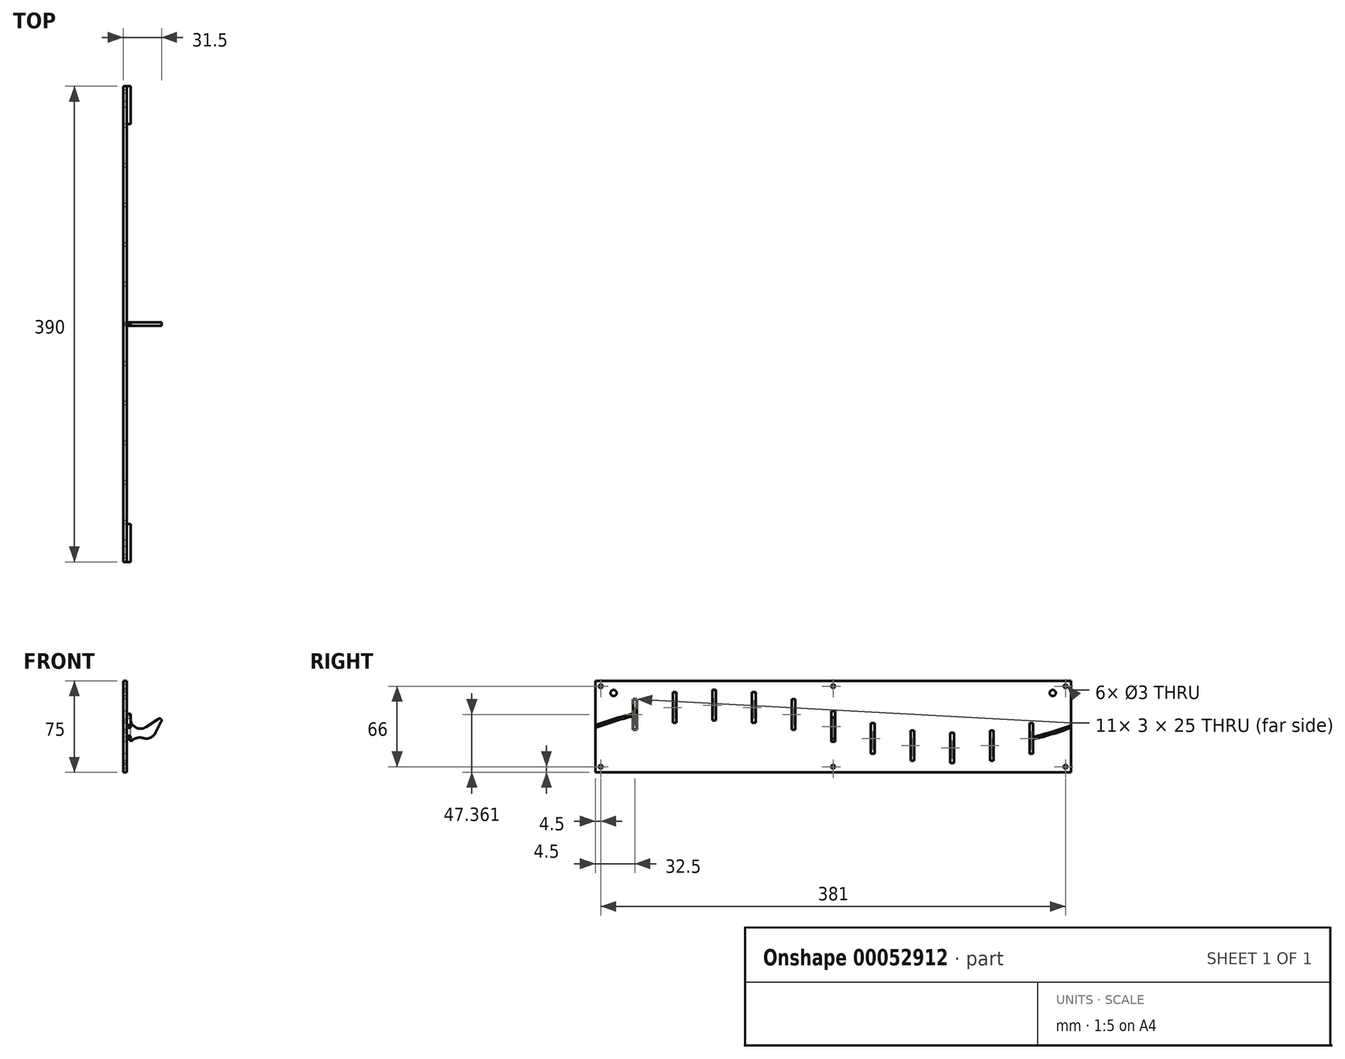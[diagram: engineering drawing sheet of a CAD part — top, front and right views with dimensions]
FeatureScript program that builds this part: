
annotation { "Feature Type Name" : "Feature", "Feature Type Description" : "" }
export const myFeature = defineFeature(function(context is Context, id is Id, definition is map)
    precondition{}
    {
        {
            assignVariable(context, id + "F0", {"name" : "Thickness", "anyValue" : 3});
        }
        {
            var Q0;
            Q0=qCreatedBy(makeId("Front.planeOp"),FACE);
            var sketch = newSketch(context, id + "F1", { "sketchPlane" : qUnion([Q0])});
            skLineSegment(sketch, "E0.top", {"start": v(0, 19) * mm, "end": v(-2, 19) * mm});
            skLineSegment(sketch, "E0.left", {"start": v(0, 0) * mm, "end": v(0, 4) * mm});
            skLineSegment(sketch, "E0.right", {"start": v(-3, 0) * mm, "end": v(-3, 3) * mm});
            skLineSegment(sketch, "E1.bottom", {"start": v(-6, 25) * mm, "end": v(-3, 25) * mm});
            skLineSegment(sketch, "E1.top", {"start": v(-6, 0) * mm, "end": v(-3, 0) * mm});
            skLineSegment(sketch, "E1.left", {"start": v(-6, 25) * mm, "end": v(-6, 0) * mm});
            skLineSegment(sketch, "E1.right", {"start": v(-3, 25) * mm, "end": v(-3, 20) * mm});
            skArc(sketch, "E2", {"start": v(-3, 20) * mm, "mid": v(-3.7, 18.3) * mm, "end": v(-2, 19) * mm});
            skLineSegment(sketch, "E3.top", {"start": v(-2, 4) * mm, "end": v(-2, 4) * mm});
            skArc(sketch, "E4", {"start": v(-2, 4) * mm, "mid": v(-3.7, 4.7) * mm, "end": v(-3, 3) * mm});
            skArc(sketch, "E5", {"start": v(0, 4) * mm, "mid": v(-1, 5) * mm, "end": v(-2, 4) * mm});
            skLineSegment(sketch, "E6.trimOffspring", {"start": v(-3, 3) * mm, "end": v(-3, 0) * mm});
            skLineSegment(sketch, "E7.trimOffspring", {"start": v(0, 19) * mm, "end": v(0, 19) * mm});
            skArc(sketch, "E8", {"start": v(0, 19) * mm, "mid": v(4.36, 11.72) * mm, "end": v(12.83, 12.13) * mm});
            skLineSegment(sketch, "E9", {"start": v(12.83, 12.13) * mm, "end": v(22.96, 18.87) * mm});
            skArc(sketch, "E10", {"start": v(25.33, 16.78) * mm, "mid": v(24.95, 18.74) * mm, "end": v(22.96, 18.87) * mm});
            skLineSegment(sketch, "E11", {"start": v(25.33, 16.78) * mm, "end": v(20.6, 7.34) * mm});
            skArc(sketch, "E12", {"start": v(10.55, 2.99) * mm, "mid": v(16.36, 3.34) * mm, "end": v(20.6, 7.34) * mm});
            skArc(sketch, "E13", {"start": v(10.55, 2.99) * mm, "mid": v(4.84, 3.02) * mm, "end": v(0, 0) * mm});
            skSolve(sketch);
        }
        {
            var Q0;
            Q0=makeQuery(id+"F1.imprint","IMPRINT",FACE,{"disambiguationData":[TD([[makeQuery(id+"F1.imprint","IMPRINT",EDGE,{"derivedFrom":sQuery(id+"F1.wireOp",EDGE,"E0.top")}),1.0]])]});
            extrude(context, id + "F2", {"entities" : qUnion([Q0]), "endBound" : BoundingType.SYMMETRIC, "depth" : (getVariable(context, 'Thickness')) * mm});
        }
        {
            var Q0;
            Q0=makeQuery(id+"F2.opExtrude","SWEPT_FACE",FACE,{"disambiguationData":[OSD([sQuery(id+"F1.wireOp",EDGE,"E1.left")])]});
            var sketch = newSketch(context, id + "F3", { "sketchPlane" : qUnion([Q0])});
            skLineSegment(sketch, "E14.bottom", {"start": v(-195, 50) * mm, "end": v(195, 50) * mm});
            skLineSegment(sketch, "E14.top", {"start": v(-195, -25) * mm, "end": v(195, -25) * mm});
            skLineSegment(sketch, "E14.left", {"start": v(-195, 50) * mm, "end": v(-195, -25) * mm});
            skLineSegment(sketch, "E14.right", {"start": v(195, 50) * mm, "end": v(195, -25) * mm});
            skLineSegment(sketch, "E15.0", {"start": v(-1.5, 25) * mm, "end": v(-1.5, 0) * mm});
            skLineSegment(sketch, "E16.0", {"start": v(1.5, 25) * mm, "end": v(-1.5, 25) * mm});
            skLineSegment(sketch, "E17.0", {"start": v(1.5, 25) * mm, "end": v(1.5, 0) * mm});
            skLineSegment(sketch, "E18.0", {"start": v(1.5, 0) * mm, "end": v(-1.5, 0) * mm});
            skLineSegment(sketch, "E19", {"start": v(-1.5, 12.5) * mm, "end": v(1.5, 12.5) * mm, "construction": true});
            skCircle(sketch, "E20", {"center": v(190.5, 45.5) * mm, "radius": 1.5 * mm});
            skCircle(sketch, "E21", {"center": v(-190.5, 45.5) * mm, "radius": 1.5 * mm});
            skCircle(sketch, "E22", {"center": v(-190.5, -20.5) * mm, "radius": 1.5 * mm});
            skCircle(sketch, "E23", {"center": v(190.5, -20.5) * mm, "radius": 1.5 * mm});
            skArc(sketch, "E24", {"start": v(195, 12.5) * mm, "mid": v(97.5, 30) * mm, "end": v(0, 12.5) * mm, "construction": true});
            skArc(sketch, "E25", {"start": v(-195, 12.5) * mm, "mid": v(-97.5, -5) * mm, "end": v(0, 12.5) * mm, "construction": true});
            skLineSegment(sketch, "E26.rect.bottom", {"start": v(63.5, 15.6) * mm, "end": v(66.5, 15.6) * mm});
            skLineSegment(sketch, "E26.rect.top", {"start": v(63.5, 40.6) * mm, "end": v(66.5, 40.6) * mm});
            skLineSegment(sketch, "E26.rect.left", {"start": v(63.5, 15.6) * mm, "end": v(63.5, 40.6) * mm});
            skLineSegment(sketch, "E26.rect.right", {"start": v(66.5, 15.6) * mm, "end": v(66.5, 40.6) * mm});
            skPoint(sketch, "E26.rect.middle", {"position": v(65, 28.1) * mm});
            skLineSegment(sketch, "E27.rect.bottom", {"start": v(96, 17.5) * mm, "end": v(99, 17.5) * mm});
            skLineSegment(sketch, "E27.rect.top", {"start": v(96, 42.5) * mm, "end": v(99, 42.5) * mm});
            skLineSegment(sketch, "E27.rect.left", {"start": v(96, 17.5) * mm, "end": v(96, 42.5) * mm});
            skLineSegment(sketch, "E27.rect.right", {"start": v(99, 17.5) * mm, "end": v(99, 42.5) * mm});
            skPoint(sketch, "E27.rect.middle", {"position": v(97.5, 30) * mm});
            skLineSegment(sketch, "E28.rect.bottom", {"start": v(128.5, 15.6) * mm, "end": v(131.5, 15.6) * mm});
            skLineSegment(sketch, "E28.rect.top", {"start": v(128.5, 40.6) * mm, "end": v(131.5, 40.6) * mm});
            skLineSegment(sketch, "E28.rect.left", {"start": v(128.5, 15.6) * mm, "end": v(128.5, 40.6) * mm});
            skLineSegment(sketch, "E28.rect.right", {"start": v(131.5, 15.6) * mm, "end": v(131.5, 40.6) * mm});
            skPoint(sketch, "E28.rect.middle", {"position": v(130, 28.1) * mm});
            skLineSegment(sketch, "E29.rect.bottom", {"start": v(161, 9.86) * mm, "end": v(164, 9.86) * mm});
            skLineSegment(sketch, "E29.rect.top", {"start": v(161, 34.86) * mm, "end": v(164, 34.86) * mm});
            skLineSegment(sketch, "E29.rect.left", {"start": v(161, 9.86) * mm, "end": v(161, 34.86) * mm});
            skLineSegment(sketch, "E29.rect.right", {"start": v(164, 9.86) * mm, "end": v(164, 34.86) * mm});
            skPoint(sketch, "E29.rect.middle", {"position": v(162.5, 22.36) * mm});
            skLineSegment(sketch, "E30.rect.bottom", {"start": v(-34, -9.86) * mm, "end": v(-31, -9.86) * mm});
            skLineSegment(sketch, "E30.rect.top", {"start": v(-34, 15.14) * mm, "end": v(-31, 15.14) * mm});
            skLineSegment(sketch, "E30.rect.left", {"start": v(-34, -9.86) * mm, "end": v(-34, 15.14) * mm});
            skLineSegment(sketch, "E30.rect.right", {"start": v(-31, -9.86) * mm, "end": v(-31, 15.14) * mm});
            skPoint(sketch, "E30.rect.middle", {"position": v(-32.5, 2.64) * mm});
            skLineSegment(sketch, "E31.rect.bottom", {"start": v(-66.5, -15.6) * mm, "end": v(-63.5, -15.6) * mm});
            skLineSegment(sketch, "E31.rect.top", {"start": v(-66.5, 9.4) * mm, "end": v(-63.5, 9.4) * mm});
            skLineSegment(sketch, "E31.rect.left", {"start": v(-66.5, -15.6) * mm, "end": v(-66.5, 9.4) * mm});
            skLineSegment(sketch, "E31.rect.right", {"start": v(-63.5, -15.6) * mm, "end": v(-63.5, 9.4) * mm});
            skPoint(sketch, "E31.rect.middle", {"position": v(-65, -3.1) * mm});
            skLineSegment(sketch, "E32.rect.bottom", {"start": v(-164, -9.86) * mm, "end": v(-161, -9.86) * mm});
            skLineSegment(sketch, "E32.rect.top", {"start": v(-164, 15.14) * mm, "end": v(-161, 15.14) * mm});
            skLineSegment(sketch, "E32.rect.left", {"start": v(-164, -9.86) * mm, "end": v(-164, 15.14) * mm});
            skLineSegment(sketch, "E32.rect.right", {"start": v(-161, -9.86) * mm, "end": v(-161, 15.14) * mm});
            skPoint(sketch, "E32.rect.middle", {"position": v(-162.5, 2.64) * mm});
            skLineSegment(sketch, "E33.rect.bottom", {"start": v(31, 9.86) * mm, "end": v(34, 9.86) * mm});
            skLineSegment(sketch, "E33.rect.top", {"start": v(31, 34.86) * mm, "end": v(34, 34.86) * mm});
            skLineSegment(sketch, "E33.rect.left", {"start": v(31, 9.86) * mm, "end": v(31, 34.86) * mm});
            skLineSegment(sketch, "E33.rect.right", {"start": v(34, 9.86) * mm, "end": v(34, 34.86) * mm});
            skPoint(sketch, "E33.rect.middle", {"position": v(32.5, 22.36) * mm});
            skLineSegment(sketch, "E34.rect.bottom", {"start": v(-99, -17.5) * mm, "end": v(-96, -17.5) * mm});
            skLineSegment(sketch, "E34.rect.top", {"start": v(-99, 7.5) * mm, "end": v(-96, 7.5) * mm});
            skLineSegment(sketch, "E34.rect.left", {"start": v(-99, -17.5) * mm, "end": v(-99, 7.5) * mm});
            skLineSegment(sketch, "E34.rect.right", {"start": v(-96, -17.5) * mm, "end": v(-96, 7.5) * mm});
            skPoint(sketch, "E34.rect.middle", {"position": v(-97.5, -5) * mm});
            skLineSegment(sketch, "E35.rect.bottom", {"start": v(-131.5, -15.6) * mm, "end": v(-128.5, -15.6) * mm});
            skLineSegment(sketch, "E35.rect.top", {"start": v(-131.5, 9.4) * mm, "end": v(-128.5, 9.4) * mm});
            skLineSegment(sketch, "E35.rect.left", {"start": v(-131.5, -15.6) * mm, "end": v(-131.5, 9.4) * mm});
            skLineSegment(sketch, "E35.rect.right", {"start": v(-128.5, -15.6) * mm, "end": v(-128.5, 9.4) * mm});
            skPoint(sketch, "E35.rect.middle", {"position": v(-130, -3.1) * mm});
            skCircle(sketch, "E36", {"center": v(0, 45.5) * mm, "radius": 1.5 * mm});
            skCircle(sketch, "E37", {"center": v(0, -20.5) * mm, "radius": 1.5 * mm});
            skCircle(sketch, "E38", {"center": v(180, 40) * mm, "radius": 2.5 * mm});
            skCircle(sketch, "E39", {"center": v(-180, 40) * mm, "radius": 2.5 * mm});
            skSolve(sketch);
        }
        {
            var Q0;
            Q0=makeQuery(id+"F3.imprint","IMPRINT",FACE,{"disambiguationData":[TD([[makeQuery(id+"F3.imprint","IMPRINT",EDGE,{"derivedFrom":sQuery(id+"F3.wireOp",EDGE,"E14.bottom")}),-1.0]])]});
            extrude(context, id + "F4", {"entities" : qUnion([Q0]), "oppositeDirection" : true, "depth" : (getVariable(context, 'Thickness')) * mm});
        }
        {
            var Q0;
            Q0=makeQuery(id+"F4.opExtrude","CAP_FACE",FACE,{"disambiguationData":[OSD([sQuery(id+"F3.wireOp",EDGE,"E14.bottom"),sQuery(id+"F3.wireOp",EDGE,"E14.top"),sQuery(id+"F3.wireOp",EDGE,"E14.left"),sQuery(id+"F3.wireOp",EDGE,"E14.right"),sQuery(id+"F3.wireOp",EDGE,"E15.0"),sQuery(id+"F3.wireOp",EDGE,"E16.0"),sQuery(id+"F3.wireOp",EDGE,"E17.0"),sQuery(id+"F3.wireOp",EDGE,"E18.0"),sQuery(id+"F3.wireOp",EDGE,"E20"),sQuery(id+"F3.wireOp",EDGE,"E21"),sQuery(id+"F3.wireOp",EDGE,"E22"),sQuery(id+"F3.wireOp",EDGE,"E23"),sQuery(id+"F3.wireOp",EDGE,"E26.rect.bottom"),sQuery(id+"F3.wireOp",EDGE,"E26.rect.top"),sQuery(id+"F3.wireOp",EDGE,"E26.rect.left"),sQuery(id+"F3.wireOp",EDGE,"E26.rect.right"),sQuery(id+"F3.wireOp",EDGE,"E27.rect.bottom"),sQuery(id+"F3.wireOp",EDGE,"E27.rect.top"),sQuery(id+"F3.wireOp",EDGE,"E27.rect.left"),sQuery(id+"F3.wireOp",EDGE,"E27.rect.right"),sQuery(id+"F3.wireOp",EDGE,"E28.rect.bottom"),sQuery(id+"F3.wireOp",EDGE,"E28.rect.top"),sQuery(id+"F3.wireOp",EDGE,"E28.rect.left"),sQuery(id+"F3.wireOp",EDGE,"E28.rect.right"),sQuery(id+"F3.wireOp",EDGE,"E29.rect.bottom"),sQuery(id+"F3.wireOp",EDGE,"E29.rect.top"),sQuery(id+"F3.wireOp",EDGE,"E29.rect.left"),sQuery(id+"F3.wireOp",EDGE,"E29.rect.right"),sQuery(id+"F3.wireOp",EDGE,"E30.rect.bottom"),sQuery(id+"F3.wireOp",EDGE,"E30.rect.top"),sQuery(id+"F3.wireOp",EDGE,"E30.rect.left"),sQuery(id+"F3.wireOp",EDGE,"E30.rect.right"),sQuery(id+"F3.wireOp",EDGE,"E31.rect.bottom"),sQuery(id+"F3.wireOp",EDGE,"E31.rect.top"),sQuery(id+"F3.wireOp",EDGE,"E31.rect.left"),sQuery(id+"F3.wireOp",EDGE,"E31.rect.right"),sQuery(id+"F3.wireOp",EDGE,"E32.rect.bottom"),sQuery(id+"F3.wireOp",EDGE,"E32.rect.top"),sQuery(id+"F3.wireOp",EDGE,"E32.rect.left"),sQuery(id+"F3.wireOp",EDGE,"E32.rect.right"),sQuery(id+"F3.wireOp",EDGE,"E33.rect.bottom"),sQuery(id+"F3.wireOp",EDGE,"E33.rect.top"),sQuery(id+"F3.wireOp",EDGE,"E33.rect.left"),sQuery(id+"F3.wireOp",EDGE,"E33.rect.right"),sQuery(id+"F3.wireOp",EDGE,"E34.rect.bottom"),sQuery(id+"F3.wireOp",EDGE,"E34.rect.top"),sQuery(id+"F3.wireOp",EDGE,"E34.rect.left"),sQuery(id+"F3.wireOp",EDGE,"E34.rect.right"),sQuery(id+"F3.wireOp",EDGE,"E35.rect.bottom"),sQuery(id+"F3.wireOp",EDGE,"E35.rect.top"),sQuery(id+"F3.wireOp",EDGE,"E35.rect.left"),sQuery(id+"F3.wireOp",EDGE,"E35.rect.right")])],"isStart":false});
            var sketch = newSketch(context, id + "F5", { "sketchPlane" : qUnion([Q0])});
            skArc(sketch, "E40.0", {"start": v(-195, 12.5) * mm, "mid": v(-97.5, 30) * mm, "end": v(0, 12.5) * mm, "construction": true});
            skArc(sketch, "E40.1", {"start": v(195, 12.5) * mm, "mid": v(97.5, -5) * mm, "end": v(0, 12.5) * mm, "construction": true});
            skArc(sketch, "E41.0", {"start": v(195, 11.43) * mm, "mid": v(179.64, 6.26) * mm, "end": v(164, 1.97) * mm});
            skArc(sketch, "E41.1", {"start": v(-195, 11.43) * mm, "mid": v(-179.64, 16.65) * mm, "end": v(-164, 20.97) * mm});
            skArc(sketch, "E42.0", {"start": v(-195, 13.57) * mm, "mid": v(-179.64, 18.74) * mm, "end": v(-164, 23.03) * mm});
            skArc(sketch, "E42.1", {"start": v(195, 13.57) * mm, "mid": v(179.64, 8.35) * mm, "end": v(164, 4.03) * mm});
            skLineSegment(sketch, "E43.rect.bottom", {"start": v(-161, 14.86) * mm, "end": v(-164, 14.86) * mm});
            skLineSegment(sketch, "E43.rect.top", {"start": v(-161, 29.86) * mm, "end": v(-164, 29.86) * mm});
            skLineSegment(sketch, "E43.rect.left", {"start": v(-161, 14.86) * mm, "end": v(-161, 21.69) * mm});
            skLineSegment(sketch, "E43.rect.right", {"start": v(-164, 14.86) * mm, "end": v(-164, 20.97) * mm});
            skPoint(sketch, "E43.rect.middle", {"position": v(-162.5, 22.36) * mm});
            skLineSegment(sketch, "E44.rect.bottom", {"start": v(-128.5, 20.6) * mm, "end": v(-131.5, 20.6) * mm});
            skLineSegment(sketch, "E44.rect.top", {"start": v(-128.5, 35.6) * mm, "end": v(-131.5, 35.6) * mm});
            skLineSegment(sketch, "E44.rect.left", {"start": v(-128.5, 20.6) * mm, "end": v(-128.5, 27.27) * mm});
            skLineSegment(sketch, "E44.rect.right", {"start": v(-131.5, 20.6) * mm, "end": v(-131.5, 26.92) * mm});
            skPoint(sketch, "E44.rect.middle", {"position": v(-130, 28.1) * mm});
            skLineSegment(sketch, "E45.rect.bottom", {"start": v(-96, 22.5) * mm, "end": v(-99, 22.5) * mm});
            skLineSegment(sketch, "E45.rect.top", {"start": v(-96, 37.5) * mm, "end": v(-99, 37.5) * mm});
            skLineSegment(sketch, "E45.rect.left", {"start": v(-96, 22.5) * mm, "end": v(-96, 29) * mm});
            skLineSegment(sketch, "E45.rect.right", {"start": v(-99, 22.5) * mm, "end": v(-99, 29) * mm});
            skPoint(sketch, "E45.rect.middle", {"position": v(-97.5, 30) * mm});
            skLineSegment(sketch, "E46.rect.bottom", {"start": v(-63.5, 20.6) * mm, "end": v(-66.5, 20.6) * mm});
            skLineSegment(sketch, "E46.rect.top", {"start": v(-63.5, 35.6) * mm, "end": v(-66.5, 35.6) * mm});
            skLineSegment(sketch, "E46.rect.left", {"start": v(-63.5, 20.6) * mm, "end": v(-63.5, 26.92) * mm});
            skLineSegment(sketch, "E46.rect.right", {"start": v(-66.5, 20.6) * mm, "end": v(-66.5, 27.27) * mm});
            skPoint(sketch, "E46.rect.middle", {"position": v(-65, 28.1) * mm});
            skLineSegment(sketch, "E47.rect.bottom", {"start": v(-31, 14.86) * mm, "end": v(-34, 14.86) * mm});
            skLineSegment(sketch, "E47.rect.top", {"start": v(-31, 29.86) * mm, "end": v(-34, 29.86) * mm});
            skLineSegment(sketch, "E47.rect.left", {"start": v(-31, 14.86) * mm, "end": v(-31, 20.97) * mm});
            skLineSegment(sketch, "E47.rect.right", {"start": v(-34, 14.86) * mm, "end": v(-34, 21.69) * mm});
            skPoint(sketch, "E47.rect.middle", {"position": v(-32.5, 22.36) * mm});
            skArc(sketch, "E48.trimOffspring", {"start": v(-161, 23.74) * mm, "mid": v(-146.32, 26.73) * mm, "end": v(-131.5, 28.94) * mm});
            skArc(sketch, "E49.trimOffspring", {"start": v(-161, 21.69) * mm, "mid": v(-146.32, 24.7) * mm, "end": v(-131.5, 26.92) * mm});
            skLineSegment(sketch, "E50.trimOffspring", {"start": v(-161, 23.74) * mm, "end": v(-161, 29.86) * mm});
            skLineSegment(sketch, "E51.trimOffspring", {"start": v(-164, 23.03) * mm, "end": v(-164, 29.86) * mm});
            skLineSegment(sketch, "E52.trimOffspring", {"start": v(-131.5, 28.94) * mm, "end": v(-131.5, 35.6) * mm});
            skArc(sketch, "E53.trimOffspring", {"start": v(-128.5, 27.27) * mm, "mid": v(-113.77, 28.53) * mm, "end": v(-99, 29) * mm});
            skLineSegment(sketch, "E54.trimOffspring", {"start": v(-128.5, 29.29) * mm, "end": v(-128.5, 35.6) * mm});
            skArc(sketch, "E55.trimOffspring", {"start": v(-128.5, 29.29) * mm, "mid": v(-113.77, 30.53) * mm, "end": v(-99, 31) * mm});
            skArc(sketch, "E56.trimOffspring", {"start": v(-96, 29) * mm, "mid": v(-81.23, 28.53) * mm, "end": v(-66.5, 27.27) * mm});
            skArc(sketch, "E57.trimOffspring", {"start": v(-96, 31) * mm, "mid": v(-81.23, 30.53) * mm, "end": v(-66.5, 29.29) * mm});
            skLineSegment(sketch, "E58.trimOffspring", {"start": v(-99, 31) * mm, "end": v(-99, 37.5) * mm});
            skLineSegment(sketch, "E59.trimOffspring", {"start": v(-96, 31) * mm, "end": v(-96, 37.5) * mm});
            skArc(sketch, "E60.trimOffspring", {"start": v(-63.5, 28.94) * mm, "mid": v(-48.68, 26.73) * mm, "end": v(-34, 23.74) * mm});
            skArc(sketch, "E61.trimOffspring", {"start": v(-63.5, 26.92) * mm, "mid": v(-48.68, 24.7) * mm, "end": v(-34, 21.69) * mm});
            skLineSegment(sketch, "E62.trimOffspring", {"start": v(-66.5, 29.29) * mm, "end": v(-66.5, 35.6) * mm});
            skLineSegment(sketch, "E63.trimOffspring", {"start": v(-63.5, 28.94) * mm, "end": v(-63.5, 35.6) * mm});
            skLineSegment(sketch, "E64.trimOffspring", {"start": v(-34, 23.74) * mm, "end": v(-34, 29.86) * mm});
            skArc(sketch, "E65.trimOffspring", {"start": v(-31, 23.03) * mm, "mid": v(-16.13, 18.98) * mm, "end": v(-1.5, 14.12) * mm});
            skLineSegment(sketch, "E66.trimOffspring", {"start": v(-31, 23.03) * mm, "end": v(-31, 29.86) * mm});
            skArc(sketch, "E67.trimOffspring", {"start": v(-31, 20.97) * mm, "mid": v(-16.13, 16.89) * mm, "end": v(-1.5, 11.99) * mm});
            skLineSegment(sketch, "E68.rect.bottom", {"start": v(1.5, 5) * mm, "end": v(-1.5, 5) * mm});
            skLineSegment(sketch, "E68.rect.top", {"start": v(1.5, 20) * mm, "end": v(-1.5, 20) * mm});
            skLineSegment(sketch, "E68.rect.left", {"start": v(1.5, 5) * mm, "end": v(1.5, 10.88) * mm});
            skLineSegment(sketch, "E68.rect.right", {"start": v(-1.5, 5) * mm, "end": v(-1.5, 11.99) * mm});
            skPoint(sketch, "E68.rect.middle", {"position": v(0, 12.5) * mm});
            skLineSegment(sketch, "E69.trimOffspring", {"start": v(-1.5, 14.12) * mm, "end": v(-1.5, 20) * mm});
            skLineSegment(sketch, "E70.trimOffspring", {"start": v(1.5, 13.01) * mm, "end": v(1.5, 20) * mm});
            skLineSegment(sketch, "E71.rect.bottom", {"start": v(34, -4.86) * mm, "end": v(31, -4.86) * mm});
            skLineSegment(sketch, "E71.rect.top", {"start": v(34, 10.14) * mm, "end": v(31, 10.14) * mm});
            skLineSegment(sketch, "E71.rect.left", {"start": v(34, -4.86) * mm, "end": v(34, 1.26) * mm});
            skLineSegment(sketch, "E71.rect.right", {"start": v(31, -4.86) * mm, "end": v(31, 1.97) * mm});
            skPoint(sketch, "E71.rect.middle", {"position": v(32.5, 2.64) * mm});
            skArc(sketch, "E72.trimOffspring", {"start": v(31, 4.03) * mm, "mid": v(16.13, 8.11) * mm, "end": v(1.5, 13.01) * mm});
            skArc(sketch, "E73.trimOffspring", {"start": v(31, 1.97) * mm, "mid": v(16.13, 6.02) * mm, "end": v(1.5, 10.88) * mm});
            skLineSegment(sketch, "E74.trimOffspring", {"start": v(34, 3.31) * mm, "end": v(34, 10.14) * mm});
            skLineSegment(sketch, "E75.trimOffspring", {"start": v(31, 4.03) * mm, "end": v(31, 10.14) * mm});
            skLineSegment(sketch, "E76.rect.bottom", {"start": v(66.5, -10.6) * mm, "end": v(63.5, -10.6) * mm});
            skLineSegment(sketch, "E76.rect.top", {"start": v(66.5, 4.4) * mm, "end": v(63.5, 4.4) * mm});
            skLineSegment(sketch, "E76.rect.left", {"start": v(66.5, -10.6) * mm, "end": v(66.5, -4.29) * mm});
            skLineSegment(sketch, "E76.rect.right", {"start": v(63.5, -10.6) * mm, "end": v(63.5, -3.94) * mm});
            skPoint(sketch, "E76.rect.middle", {"position": v(65, -3.1) * mm});
            skArc(sketch, "E77.trimOffspring", {"start": v(63.5, -1.92) * mm, "mid": v(48.68, 0.3) * mm, "end": v(34, 3.31) * mm});
            skArc(sketch, "E78.trimOffspring", {"start": v(63.5, -3.94) * mm, "mid": v(48.68, -1.73) * mm, "end": v(34, 1.26) * mm});
            skLineSegment(sketch, "E79.trimOffspring", {"start": v(63.5, -1.92) * mm, "end": v(63.5, 4.4) * mm});
            skLineSegment(sketch, "E80.trimOffspring", {"start": v(66.5, -2.27) * mm, "end": v(66.5, 4.4) * mm});
            skLineSegment(sketch, "E81.rect.bottom", {"start": v(99, -12.5) * mm, "end": v(96, -12.5) * mm});
            skLineSegment(sketch, "E81.rect.top", {"start": v(99, 2.5) * mm, "end": v(96, 2.5) * mm});
            skLineSegment(sketch, "E81.rect.left", {"start": v(99, -12.5) * mm, "end": v(99, -6) * mm});
            skLineSegment(sketch, "E81.rect.right", {"start": v(96, -12.5) * mm, "end": v(96, -6) * mm});
            skPoint(sketch, "E81.rect.middle", {"position": v(97.5, -5) * mm});
            skLineSegment(sketch, "E82.trimOffspring", {"start": v(96, -4) * mm, "end": v(96, 2.5) * mm});
            skArc(sketch, "E83.trimOffspring", {"start": v(96, -6) * mm, "mid": v(81.23, -5.53) * mm, "end": v(66.5, -4.29) * mm});
            skArc(sketch, "E84.trimOffspring", {"start": v(96, -4) * mm, "mid": v(81.23, -3.53) * mm, "end": v(66.5, -2.27) * mm});
            skLineSegment(sketch, "E85.trimOffspring", {"start": v(99, -4) * mm, "end": v(99, 2.5) * mm});
            skLineSegment(sketch, "E86.rect.bottom", {"start": v(131.5, -10.6) * mm, "end": v(128.5, -10.6) * mm});
            skLineSegment(sketch, "E86.rect.top", {"start": v(131.5, 4.4) * mm, "end": v(128.5, 4.4) * mm});
            skLineSegment(sketch, "E86.rect.left", {"start": v(131.5, -10.6) * mm, "end": v(131.5, -3.94) * mm});
            skLineSegment(sketch, "E86.rect.right", {"start": v(128.5, -10.6) * mm, "end": v(128.5, -4.29) * mm});
            skPoint(sketch, "E86.rect.middle", {"position": v(130, -3.1) * mm});
            skArc(sketch, "E87.trimOffspring", {"start": v(128.5, -2.27) * mm, "mid": v(113.77, -3.53) * mm, "end": v(99, -4) * mm});
            skLineSegment(sketch, "E88.trimOffspring", {"start": v(128.5, -2.27) * mm, "end": v(128.5, 4.4) * mm});
            skArc(sketch, "E89.trimOffspring", {"start": v(128.5, -4.29) * mm, "mid": v(113.77, -5.53) * mm, "end": v(99, -6) * mm});
            skLineSegment(sketch, "E90.trimOffspring", {"start": v(131.5, -1.92) * mm, "end": v(131.5, 4.4) * mm});
            skLineSegment(sketch, "E91.rect.bottom", {"start": v(164, -4.86) * mm, "end": v(161, -4.86) * mm});
            skLineSegment(sketch, "E91.rect.top", {"start": v(164, 10.14) * mm, "end": v(161, 10.14) * mm});
            skLineSegment(sketch, "E91.rect.left", {"start": v(164, -4.86) * mm, "end": v(164, 1.97) * mm});
            skLineSegment(sketch, "E91.rect.right", {"start": v(161, -4.86) * mm, "end": v(161, 1.26) * mm});
            skPoint(sketch, "E91.rect.middle", {"position": v(162.5, 2.64) * mm});
            skArc(sketch, "E92.trimOffspring", {"start": v(161, 3.31) * mm, "mid": v(146.32, 0.3) * mm, "end": v(131.5, -1.92) * mm});
            skLineSegment(sketch, "E93.trimOffspring", {"start": v(161, 3.31) * mm, "end": v(161, 10.14) * mm});
            skArc(sketch, "E94.trimOffspring", {"start": v(161, 1.26) * mm, "mid": v(146.32, -1.73) * mm, "end": v(131.5, -3.94) * mm});
            skLineSegment(sketch, "E95.trimOffspring", {"start": v(164, 4.03) * mm, "end": v(164, 10.14) * mm});
            skLineSegment(sketch, "E96", {"start": v(195, 11.43) * mm, "end": v(195, -25) * mm});
            skLineSegment(sketch, "E97", {"start": v(195, -25) * mm, "end": v(-195, -25) * mm});
            skLineSegment(sketch, "E98", {"start": v(-195, -25) * mm, "end": v(-195, 11.43) * mm});
            skLineSegment(sketch, "E99", {"start": v(-195, 13.57) * mm, "end": v(-195, 50) * mm});
            skLineSegment(sketch, "E100", {"start": v(-195, 50) * mm, "end": v(195, 50) * mm});
            skLineSegment(sketch, "E101", {"start": v(195, 50) * mm, "end": v(195, 13.57) * mm});
            skCircle(sketch, "E102.0", {"center": v(-190.5, 45.5) * mm, "radius": 1.5 * mm});
            skCircle(sketch, "E103.0", {"center": v(-190.5, -20.5) * mm, "radius": 1.5 * mm});
            skCircle(sketch, "E104.0", {"center": v(190.5, 45.5) * mm, "radius": 1.5 * mm});
            skCircle(sketch, "E105.0", {"center": v(190.5, -20.5) * mm, "radius": 1.5 * mm});
            skCircle(sketch, "E106.0", {"center": v(0, 45.5) * mm, "radius": 1.5 * mm});
            skPoint(sketch, "E107.0", {"position": v(0, -20.5) * mm});
            skCircle(sketch, "E108.0", {"center": v(0, -20.5) * mm, "radius": 1.5 * mm});
            skCircle(sketch, "E109.0", {"center": v(-180, 40) * mm, "radius": 2.5 * mm});
            skCircle(sketch, "E110.0", {"center": v(180, 40) * mm, "radius": 2.5 * mm});
            skSolve(sketch);
        }
        {
            var Q0;
            Q0=makeQuery(id+"F5.imprint","IMPRINT",FACE,{"disambiguationData":[TD([[makeQuery(id+"F5.imprint","IMPRINT",EDGE,{"derivedFrom":sQuery(id+"F5.wireOp",EDGE,"E42.0")}),1.0]])]});
            var Q1;
            Q1=makeQuery(id+"F5.imprint","IMPRINT",FACE,{"disambiguationData":[TD([[makeQuery(id+"F5.imprint","IMPRINT",EDGE,{"derivedFrom":sQuery(id+"F5.wireOp",EDGE,"E41.0")}),1.0]])]});
            extrude(context, id + "F6", {"entities" : qUnion([Q0, Q1]), "depth" : (getVariable(context, 'Thickness')) * mm});
        }
    });
